# Revit family: Drain_Floor_Medium-Duty_Adjustable_Zurn-Z1726-1
name_source: partatom
category: Plumbing Fixtures
units: mm (PartAtom-declared; Revit-internal decimal feet)

## family parameters
Always vertical = Yes
Cut with Voids When Loaded = No
Maintain Annotation Orientation = No
OmniClass Number = 23.45.55.21
OmniClass Title = Drains (Wastes)
Part Type = Normal
Room Calculation Point = No
Round Connector Dimension = Use Radius
Shared = No
Work Plane-Based = No

## types (1)
- Load Family Type Catalog
    10 Model lines slots = Yes
    10_Strainer Slots = Yes
    5_Strainer Slots = Yes
    6_Strainer Slots = Yes
    7_Strainer Slots = Yes
    8_Strainer Slots = Yes
    A1_Outlet Radius Interior = 3.18 "
    A2_Outlet Radius Exterior = 3.31 "
    A_Nominal Dia = 6 "
    A_Nominal Radius = 3 "
    Anno Strainer constrain = 0.88 "
    Anno_Outlet Dia Exterior = 6.63 "
    Anno_Strainer Dia Exterior = 10 "
    Approx. Weight (lbs) = 27
    Assembly Code = D2030300
    B1_Strainer Interior Radius = 4.84 "
    B2_Strainer Exterior Radius = 5 "
    B_Strainer Dia = 10 "
    Body = Steel-Zurn-Stainless-304-Polished-Silver
    Bottom Connector Constraint = 1.34 "
    Default Elevation = 20 "
    Description = Adjustable Floor Drain Medium Duty With Round Top
    E_Body Height = 2.88 "
    Inner Diameter = 6.36 "
    Main Material = Steel-Zurn-Stainless-304
    Manufacturer = Zurn Water, LLC
    Manufacturer Brand = Zurn
    Model = Z1726
    Modified Date = 08/28/2025
    Outside Diameter = 6.63 "
    Product Documentation Link = https://files.zurn.com
    Product Page URL = https://www.zurn.com
    Product data URL = https://www.bimobject.com
    Slot distance Horizontal = 1.94 "
    Slot distance Vertical = 1.61 "
    Type Comments = Z1726-6 Inch Butt-Weld 10” Dia. Top (Sch.10)
    URL = www.zurn.com
    Waste Connection = Yes

## geometry (parser evidence)
native form markers: Sweep x3
no freeform markers — native parametric forms only
